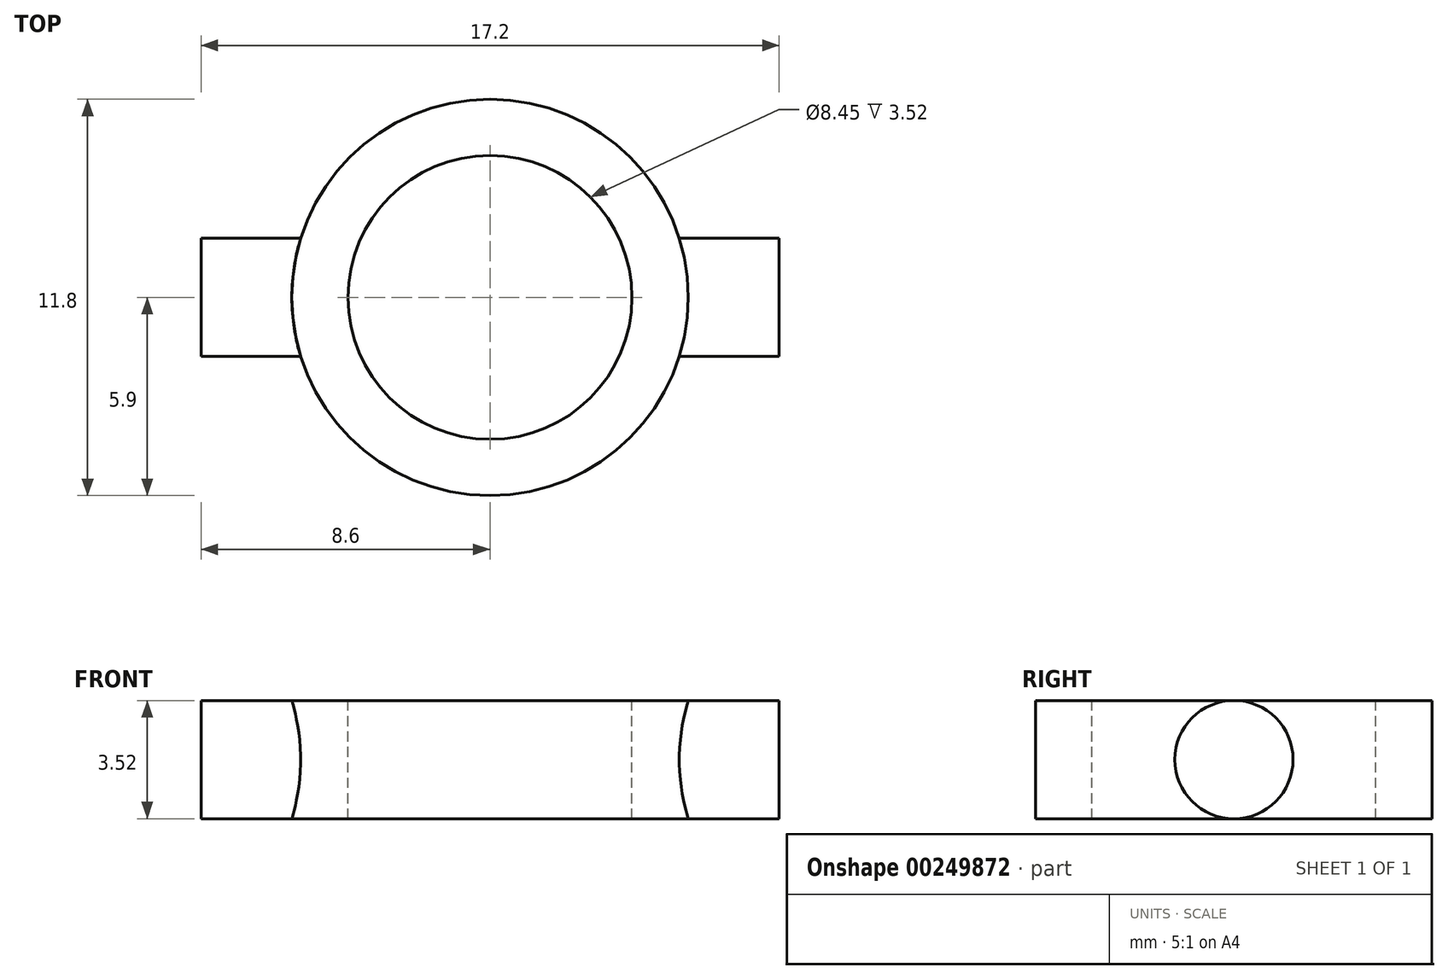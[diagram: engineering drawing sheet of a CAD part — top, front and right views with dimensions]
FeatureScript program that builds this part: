
annotation { "Feature Type Name" : "Feature", "Feature Type Description" : "" }
export const myFeature = defineFeature(function(context is Context, id is Id, definition is map)
    precondition{}
    {
        {
            var Q0;
            Q0=qCreatedBy(makeId("Right.planeOp"),FACE);
            var sketch = newSketch(context, id + "F0", { "sketchPlane" : qUnion([Q0])});
            skCircle(sketch, "E0", {"center": v(0, 1.76) * mm, "radius": 1.76 * mm});
            skSolve(sketch);
        }
        {
            var Q0;
            Q0 = qSketchRegion(id + "F0", true);
            extrude(context, id + "F1", {"entities" : qUnion([Q0]), "depth" : 8.6 * mm, "hasSecondDirection" : true, "secondDirectionOppositeDirection" : true, "secondDirectionDepth" : 8.6 * mm});
        }
        {
            var Q0;
            Q0=qCreatedBy(makeId("Top.planeOp"),FACE);
            var sketch = newSketch(context, id + "F2", { "sketchPlane" : qUnion([Q0])});
            skCircle(sketch, "E1", {"center": v(0, 0) * mm, "radius": 5.9 * mm});
            skSolve(sketch);
        }
        {
            var Q0;
            Q0 = qSketchRegion(id + "F2", true);
            extrude(context, id + "F3", {"entities" : qUnion([Q0]), "operationType" : NewBodyOperationType.ADD, "depth" : 3.52 * mm});
        }
        {
            var Q0;
            Q0=makeQuery(id+"F3.opExtrude","CAP_FACE",FACE,{"disambiguationData":[OSD([sQuery(id+"F2.wireOp",EDGE,"E1")])],"isStart":false});
            var sketch = newSketch(context, id + "F4", { "sketchPlane" : qUnion([Q0])});
            skCircle(sketch, "E2", {"center": v(0, 0) * mm, "radius": 4.22 * mm});
            skSolve(sketch);
        }
        {
            var Q0;
            Q0 = qSketchRegion(id + "F4", true);
            extrude(context, id + "F5", {"entities" : qUnion([Q0]), "operationType" : NewBodyOperationType.REMOVE, "oppositeDirection" : true, "depth" : 5 * mm});
        }
    });
